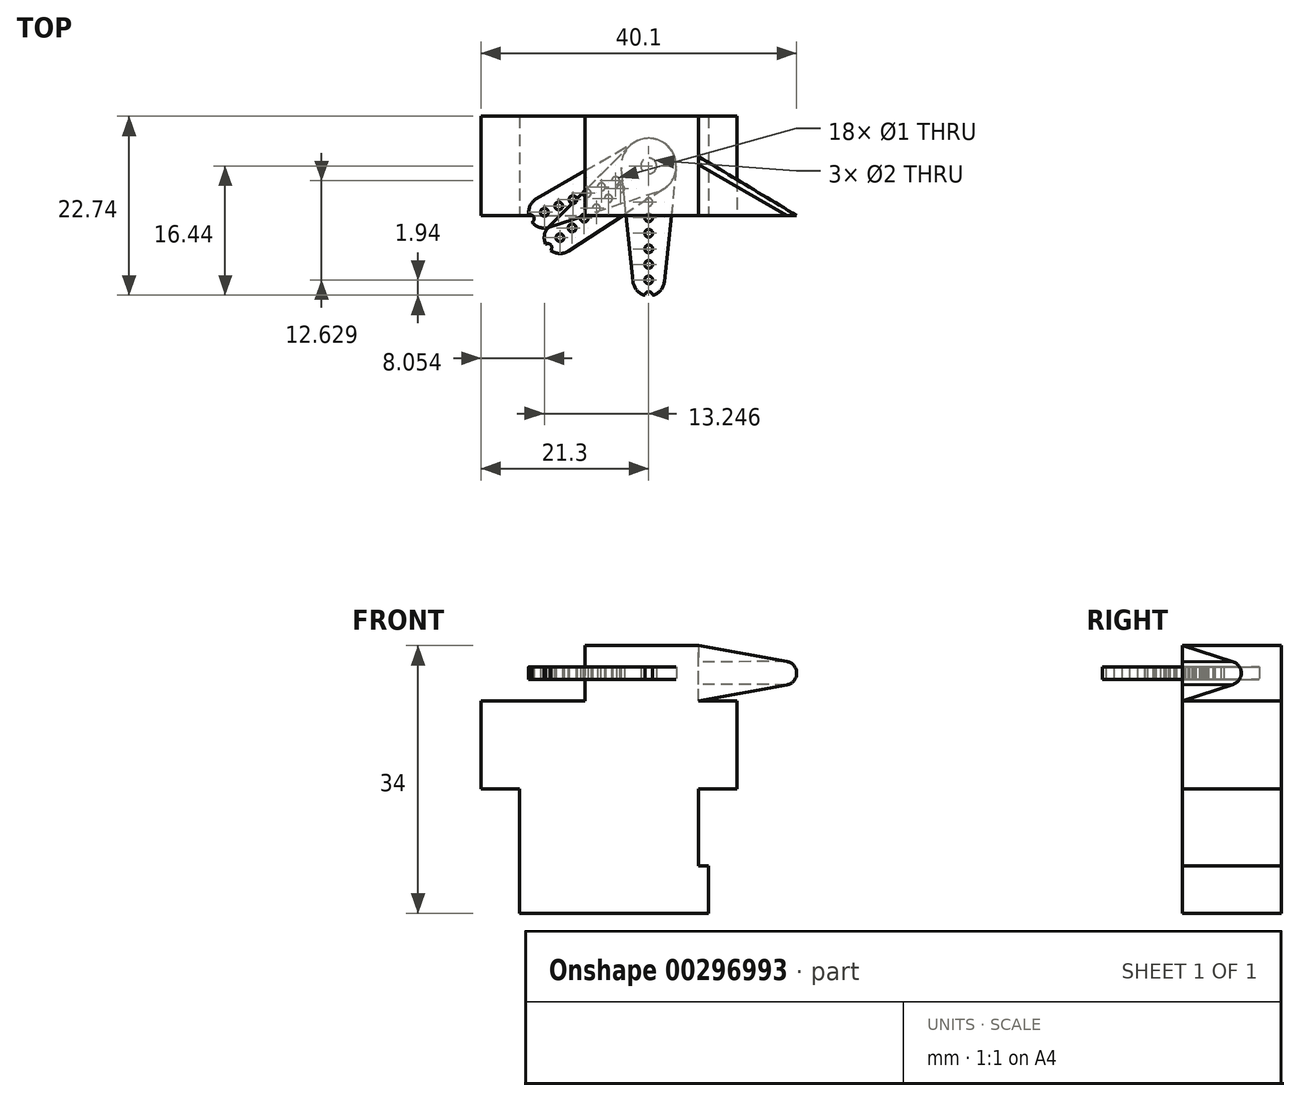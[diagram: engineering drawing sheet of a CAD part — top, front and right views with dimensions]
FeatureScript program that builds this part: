
annotation { "Feature Type Name" : "Feature", "Feature Type Description" : "" }
export const myFeature = defineFeature(function(context is Context, id is Id, definition is map)
    precondition{}
    {
        {
            var Q0;
            Q0=qCreatedBy(makeId("Front.planeOp"),FACE);
            var sketch = newSketch(context, id + "F0", { "sketchPlane" : qUnion([Q0])});
            skLineSegment(sketch, "E0.bottom", {"start": v(0, 6.8) * mm, "end": v(22.7, 6.8) * mm});
            skLineSegment(sketch, "E0.top", {"start": v(0, -15.8) * mm, "end": v(22.7, -15.8) * mm});
            skLineSegment(sketch, "E0.left", {"start": v(0, 6.8) * mm, "end": v(0, -15.8) * mm});
            skLineSegment(sketch, "E0.right", {"start": v(22.7, 6.8) * mm, "end": v(22.7, -15.8) * mm});
            skLineSegment(sketch, "E1.bottom", {"start": v(-4.9, 2.4) * mm, "end": v(27.6, 2.4) * mm});
            skLineSegment(sketch, "E1.top", {"start": v(-4.9, 0) * mm, "end": v(27.6, 0) * mm});
            skLineSegment(sketch, "E1.left", {"start": v(-4.9, 2.4) * mm, "end": v(-4.9, 0) * mm});
            skLineSegment(sketch, "E1.right", {"start": v(27.6, 2.4) * mm, "end": v(27.6, 0) * mm});
            skLineSegment(sketch, "E2.top", {"start": v(8.3, 6.8) * mm, "end": v(22.7, 6.8) * mm});
            skLineSegment(sketch, "E2.left", {"start": v(8.3, 11.2) * mm, "end": v(8.3, 6.8) * mm});
            skLineSegment(sketch, "E2.right", {"start": v(22.7, 11.2) * mm, "end": v(22.7, 6.8) * mm});
            skLineSegment(sketch, "E3", {"start": v(11.35, -15.8) * mm, "end": v(11.35, 0) * mm, "construction": true});
            skPoint(sketch, "E4", {"position": v(0, 0) * mm});
            skLineSegment(sketch, "E5", {"start": v(22.7, -15.8) * mm, "end": v(24, -15.8) * mm});
            skLineSegment(sketch, "E6", {"start": v(24, -15.8) * mm, "end": v(24, -9.8) * mm});
            skLineSegment(sketch, "E7", {"start": v(24, -9.8) * mm, "end": v(22.7, -9.8) * mm});
            skLineSegment(sketch, "E8", {"start": v(8.3, 18.2) * mm, "end": v(22.7, 18.2) * mm});
            skLineSegment(sketch, "E9", {"start": v(22.7, 18.2) * mm, "end": v(22.7, 11.2) * mm});
            skLineSegment(sketch, "E10", {"start": v(22.7, 11.2) * mm, "end": v(33.97, 13.22) * mm});
            skLineSegment(sketch, "E11", {"start": v(22.7, 18.2) * mm, "end": v(33.97, 16.18) * mm});
            skArc(sketch, "E12", {"start": v(33.97, 13.22) * mm, "mid": v(35.2, 14.7) * mm, "end": v(33.97, 16.18) * mm});
            skLineSegment(sketch, "E13", {"start": v(16.4, 14.7) * mm, "end": v(22.7, 14.7) * mm, "construction": true});
            skLineSegment(sketch, "E14", {"start": v(8.3, 11.2) * mm, "end": v(8.3, 18.2) * mm});
            skLineSegment(sketch, "E15", {"start": v(8.3, 11.2) * mm, "end": v(22.7, 11.2) * mm});
            skSolve(sketch);
        }
        {
            var Q0;
            {var subQ5=sQuery(id+"F0.wireOp",EDGE,"E0.bottom");Q0=makeQuery(id+"F0.imprint","IMPRINT",FACE,{"disambiguationData":[TD([[makeQuery(id+"F0.imprint","IMPRINT",EDGE,{"derivedFrom":subQ5}),-1.0]])]});}
            var Q1;
            {var subQ5=sQuery(id+"F0.wireOp",EDGE,"E1.left");Q1=makeQuery(id+"F0.imprint","IMPRINT",FACE,{"disambiguationData":[TD([[makeQuery(id+"F0.imprint","IMPRINT",EDGE,{"derivedFrom":subQ5}),1.0]])]});}
            var Q2;
            {var subQ0=sQuery(id+"F0.wireOp",EDGE,"E1.bottom");var subQ1=sQuery(id+"F0.wireOp",EDGE,"E0.left");var subQ2=makeQuery(id+"F0.imprint","INTERSECT",VERTEX,{"derivedFrom":[subQ1,subQ0]});Q2=makeQuery(id+"F0.imprint","IMPRINT",FACE,{"disambiguationData":[TD([[makeQuery(id+"F0.imprint","IMPRINT",EDGE,{"disambiguationData":[TD([[subQ2,-1.0]])],"derivedFrom":subQ1}),1.0]])]});}
            var Q3;
            Q3=makeQuery(id+"F0.imprint","IMPRINT",FACE,{"disambiguationData":[TD([[makeQuery(id+"F0.imprint","IMPRINT",EDGE,{"derivedFrom":sQuery(id+"F0.wireOp",EDGE,"E2.bottom")}),-1.0]])]});
            var Q4;
            {var subQ5=sQuery(id+"F0.wireOp",EDGE,"E1.right");Q4=makeQuery(id+"F0.imprint","IMPRINT",FACE,{"disambiguationData":[TD([[makeQuery(id+"F0.imprint","IMPRINT",EDGE,{"derivedFrom":subQ5}),-1.0]])]});}
            var Q5;
            {var subQ0=sQuery(id+"F0.wireOp",EDGE,"E0.top");Q5=makeQuery(id+"F0.imprint","IMPRINT",FACE,{"disambiguationData":[TD([[makeQuery(id+"F0.imprint","IMPRINT",EDGE,{"derivedFrom":subQ0}),1.0]])]});}
            var Q6;
            {var subQ0=sQuery(id+"F0.wireOp",EDGE,"E2.bottom");Q6=makeQuery(id+"F0.imprint","IMPRINT",FACE,{"disambiguationData":[TD([[makeQuery(id+"F0.imprint","IMPRINT",EDGE,{"derivedFrom":subQ0}),1.0]])]});}
            var Q7;
            Q7=makeQuery(id+"F0.imprint","IMPRINT",FACE,{"disambiguationData":[TD([[makeQuery(id+"F0.imprint","IMPRINT",EDGE,{"derivedFrom":sQuery(id+"F0.wireOp",EDGE,"E2.top")}),1.0]])]});
            extrude(context, id + "F1", {"entities" : qUnion([Q0, Q1, Q2, Q3, Q4, Q5, Q6, Q7]), "oppositeDirection" : true, "depth" : 12.6 * mm, "offsetDistance" : 25 * mm});
        }
        {
            var Q0;
            Q0=qCreatedBy(makeId("Top.planeOp"),FACE);
            var sketch = newSketch(context, id + "F2", { "sketchPlane" : qUnion([Q0])});
            skLineSegment(sketch, "E16.bottom", {"start": v(-4.9, 0) * mm, "end": v(27.6, 0) * mm});
            skLineSegment(sketch, "E16.top", {"start": v(-4.9, 12.6) * mm, "end": v(27.6, 12.6) * mm});
            skLineSegment(sketch, "E16.left", {"start": v(-4.9, 12.6) * mm, "end": v(-4.9, 0) * mm});
            skLineSegment(sketch, "E16.right", {"start": v(27.6, 12.6) * mm, "end": v(27.6, 0) * mm});
            skSolve(sketch);
        }
        {
            var Q0;
            Q0=qCreatedBy(makeId("Top.planeOp"),FACE);
            var Q1;
            Q1=sQuery(id+"F0.wireOp",VERTEX,"E13.start");
            cPlane(context, id + "F3", {"entities" : qUnion([Q0, Q1]), "cplaneType" : CPlaneType.PLANE_POINT, "offset" : 25 * mm, "width" : 150 * mm, "height" : 150 * mm});
        }
        {
            var Q0;
            Q0=qCreatedBy(id+"F3.planeOp",FACE);
            var sketch = newSketch(context, id + "F4", { "sketchPlane" : qUnion([Q0])});
            skLineSegment(sketch, "E17", {"start": v(16.4, 0) * mm, "end": v(16.4, 12.6) * mm, "construction": true});
            skPoint(sketch, "E18", {"position": v(16.4, 6.3) * mm});
            skPoint(sketch, "E19.0", {"position": v(16.4, 0) * mm});
            skLineSegment(sketch, "E20", {"start": v(16.4, 6.3) * mm, "end": v(16.4, -8.2) * mm});
            skLineSegment(sketch, "E21", {"start": v(16.4, 6.3) * mm, "end": v(16.4, 1.7) * mm});
            skCircle(sketch, "E22", {"center": v(16.4, 1.7) * mm, "radius": 0.5 * mm});
            skArc(sketch, "E23", {"start": v(18.39, -8.4) * mm, "mid": v(16.4, -10.2) * mm, "end": v(14.41, -8.4) * mm});
            skArc(sketch, "E24", {"start": v(19.88, 5.94) * mm, "mid": v(16.4, 9.8) * mm, "end": v(12.92, 5.94) * mm});
            skLineSegment(sketch, "E25", {"start": v(19.88, 5.94) * mm, "end": v(18.39, -8.4) * mm});
            skLineSegment(sketch, "E26", {"start": v(14.41, -8.4) * mm, "end": v(12.92, 5.94) * mm});
            skCircle(sketch, "E27", {"center": v(16.4, 6.3) * mm, "radius": 1 * mm});
            skCircle(sketch, "E28.1.0.0", {"center": v(16.4, -0.28) * mm, "radius": 0.5 * mm});
            skCircle(sketch, "E28.2.0.0", {"center": v(16.4, -2.26) * mm, "radius": 0.5 * mm});
            skLineSegment(sketch, "E28.direction1", {"start": v(16.4, 1.7) * mm, "end": v(16.4, -0.28) * mm, "construction": true});
            skCircle(sketch, "E29.0.3.0", {"center": v(16.4, -4.24) * mm, "radius": 0.5 * mm});
            skCircle(sketch, "E29.0.4.0", {"center": v(16.4, -6.22) * mm, "radius": 0.5 * mm});
            skCircle(sketch, "E29.0.5.0", {"center": v(16.4, -8.2) * mm, "radius": 0.5 * mm});
            skCircle(sketch, "E30.0.6.0", {"center": v(16.4, -10.18) * mm, "radius": 0.5 * mm});
            skLineSegment(sketch, "E31", {"start": v(16.4, 6.3) * mm, "end": v(3.15, 0.4) * mm, "construction": true});
            skLineSegment(sketch, "E32", {"start": v(16.4, 6.3) * mm, "end": v(5.13, -2.83) * mm, "construction": true});
            skSolve(sketch);
        }
        {
            var Q0;
            {var subQ1=sQuery(id+"F0.wireOp",EDGE,"E0.top");Q0=makeQuery(id+"F0.imprint","IMPRINT",FACE,{"disambiguationData":[TD([[makeQuery(id+"F0.imprint","IMPRINT",EDGE,{"derivedFrom":subQ1}),1.0]])]});}
            var Q1;
            {var subQ1=sQuery(id+"F0.wireOp",EDGE,"E0.bottom");Q1=makeQuery(id+"F0.imprint","IMPRINT",FACE,{"disambiguationData":[TD([[makeQuery(id+"F0.imprint","IMPRINT",EDGE,{"derivedFrom":subQ1}),-1.0]])]});}
            var Q2;
            {var subQ0=sQuery(id+"F0.wireOp",EDGE,"E1.bottom");var subQ1=sQuery(id+"F0.wireOp",EDGE,"E0.left");var subQ2=makeQuery(id+"F0.imprint","INTERSECT",VERTEX,{"derivedFrom":[subQ1,subQ0]});Q2=makeQuery(id+"F0.imprint","IMPRINT",FACE,{"disambiguationData":[TD([[makeQuery(id+"F0.imprint","IMPRINT",EDGE,{"disambiguationData":[TD([[subQ2,-1.0]])],"derivedFrom":subQ1}),1.0]])]});}
            var Q3;
            Q3=makeQuery(id+"F0.imprint","IMPRINT",FACE,{"disambiguationData":[TD([[makeQuery(id+"F0.imprint","IMPRINT",EDGE,{"derivedFrom":sQuery(id+"F0.wireOp",EDGE,"E2.bottom")}),-1.0]])]});
            var Q4;
            {var subQ0=sQuery(id+"F0.wireOp",EDGE,"E5");Q4=makeQuery(id+"F0.imprint","IMPRINT",FACE,{"disambiguationData":[TD([[makeQuery(id+"F0.imprint","IMPRINT",EDGE,{"derivedFrom":subQ0}),1.0]])]});}
            var Q5;
            {var subQ0=sQuery(id+"F0.wireOp",EDGE,"E9");var subQ5=sQuery(id+"F0.wireOp",EDGE,"E15");var subQ6=makeQuery(id+"F0.imprint","INTERSECT",VERTEX,{"derivedFrom":[subQ0,subQ5]});Q5=makeQuery(id+"F0.imprint","IMPRINT",FACE,{"disambiguationData":[TD([[makeQuery(id+"F0.imprint","IMPRINT",EDGE,{"disambiguationData":[TD([[subQ6,1.0]])],"derivedFrom":subQ5}),1.0]])]});}
            var Q6;
            {var subQ0=sQuery(id+"F0.wireOp",EDGE,"E9");var subQ5=sQuery(id+"F0.wireOp",EDGE,"E15");var subQ6=makeQuery(id+"F0.imprint","INTERSECT",VERTEX,{"derivedFrom":[subQ0,subQ5]});Q6=makeQuery(id+"F0.imprint","IMPRINT",FACE,{"disambiguationData":[TD([[makeQuery(id+"F0.imprint","IMPRINT",EDGE,{"disambiguationData":[TD([[subQ6,1.0]])],"derivedFrom":subQ5}),-1.0]])]});}
            var Q7;
            {var subQ0=sQuery(id+"F0.wireOp",EDGE,"E14");var subQ5=sQuery(id+"F0.wireOp",EDGE,"E15");var subQ6=makeQuery(id+"F0.imprint","INTERSECT",VERTEX,{"derivedFrom":[subQ0,subQ5]});Q7=makeQuery(id+"F0.imprint","IMPRINT",FACE,{"disambiguationData":[TD([[makeQuery(id+"F0.imprint","IMPRINT",EDGE,{"disambiguationData":[TD([[subQ6,-1.0]])],"derivedFrom":subQ5}),-1.0]])]});}
            var Q8;
            {var subQ0=sQuery(id+"F0.wireOp",EDGE,"E14");var subQ1=sQuery(id+"F0.wireOp",EDGE,"E8");var subQ2=makeQuery(id+"F0.imprint","INTERSECT",VERTEX,{"derivedFrom":[subQ1,subQ0]});Q8=makeQuery(id+"F0.imprint","IMPRINT",FACE,{"disambiguationData":[TD([[makeQuery(id+"F0.imprint","IMPRINT",EDGE,{"disambiguationData":[TD([[subQ2,-1.0]])],"derivedFrom":subQ1}),-1.0]])]});}
            var Q9;
            Q9=makeQuery(id+"F1.opExtrude","CAP_FACE",FACE,{"disambiguationData":[OSD([sQuery(id+"F0.wireOp",EDGE,"E0.bottom"),sQuery(id+"F0.wireOp",EDGE,"E0.top"),sQuery(id+"F0.wireOp",EDGE,"E0.left"),sQuery(id+"F0.wireOp",EDGE,"E0.right"),sQuery(id+"F0.wireOp",EDGE,"E1.bottom"),sQuery(id+"F0.wireOp",EDGE,"E1.top"),sQuery(id+"F0.wireOp",EDGE,"E1.left"),sQuery(id+"F0.wireOp",EDGE,"E1.right"),sQuery(id+"F0.wireOp",EDGE,"E2.bottom"),sQuery(id+"F0.wireOp",EDGE,"E2.left"),sQuery(id+"F0.wireOp",EDGE,"E2.right")])],"isStart":false});
            extrude(context, id + "F5", {"entities" : qUnion([Q0, Q1, Q2, Q3, Q4, Q5, Q6, Q7, Q8]), "endBound" : BoundingType.UP_TO_SURFACE, "oppositeDirection" : true, "depth" : 25 * mm, "endBoundEntityFace" : qUnion([Q9]), "offsetDistance" : 25 * mm});
        }
        {
            var Q0;
            Q0=makeQuery(id+"F5.opExtrude","SWEPT_BODY",BODY,{"disambiguationData":[OSD([sQuery(id+"F0.wireOp",EDGE,"E0.bottom"),sQuery(id+"F0.wireOp",EDGE,"E0.top"),sQuery(id+"F0.wireOp",EDGE,"E0.left"),sQuery(id+"F0.wireOp",EDGE,"E0.right"),sQuery(id+"F0.wireOp",EDGE,"E2.left"),sQuery(id+"F0.wireOp",EDGE,"E2.right"),sQuery(id+"F0.wireOp",EDGE,"E5"),sQuery(id+"F0.wireOp",EDGE,"E6"),sQuery(id+"F0.wireOp",EDGE,"E7"),sQuery(id+"F0.wireOp",EDGE,"E8"),sQuery(id+"F0.wireOp",EDGE,"E9"),sQuery(id+"F0.wireOp",EDGE,"E14")])]});
            transform(context, id + "F6", {"entities" : qUnion([Q0]), "transformType" : TransformType.COPY});
        }
        {
            var Q0;
            {var subQ0=sQuery(id+"F0.wireOp",EDGE,"E1.top");Q0=makeQuery(id+"F1.opExtrude","SWEPT_FACE",FACE,{"disambiguationData":[OSD([subQ0]),TDD([makeQuery(id+"F0.imprint","IMPRINT",EDGE,{"disambiguationData":[TD([[makeQuery(id+"F0.imprint","INTERSECT",VERTEX,{"derivedFrom":[subQ0,sQuery(id+"F0.wireOp",EDGE,"E1.left")]}),-1.0]])],"derivedFrom":subQ0})])]});}
            var Q1;
            {var subQ0=sQuery(id+"F0.wireOp",EDGE,"E1.top");Q1=makeQuery(id+"F1.opExtrude","SWEPT_FACE",FACE,{"disambiguationData":[OSD([subQ0]),TDD([makeQuery(id+"F0.imprint","IMPRINT",EDGE,{"disambiguationData":[TD([[makeQuery(id+"F0.imprint","INTERSECT",VERTEX,{"derivedFrom":[subQ0,sQuery(id+"F0.wireOp",EDGE,"E1.right")]}),1.0]])],"derivedFrom":subQ0})])]});}
            var Q2;
            Q2=makeQuery(id+"F1.opExtrude","SWEPT_FACE",FACE,{"disambiguationData":[OSD([sQuery(id+"F0.wireOp",EDGE,"E0.bottom")])]});
            var Q3;
            Q3=sQuery(id+"F0.wireOp",VERTEX,"E2.right.start");
            extrude(context, id + "F7", {"entities" : qUnion([Q0, Q1, Q2]), "operationType" : NewBodyOperationType.ADD, "endBound" : BoundingType.UP_TO_VERTEX, "oppositeDirection" : true, "depth" : 25 * mm, "endBoundEntityVertex" : qUnion([Q3]), "offsetDistance" : 25 * mm});
        }
        {
            var Q0;
            Q0=makeQuery(id+"F1.opExtrude","SWEPT_FACE",FACE,{"disambiguationData":[OSD([sQuery(id+"F0.wireOp",EDGE,"E0.right"),sQuery(id+"F0.wireOp",EDGE,"E2.right")])]});
            var sketch = newSketch(context, id + "F8", { "sketchPlane" : qUnion([Q0])});
            skLineSegment(sketch, "E33", {"start": v(0, 14.7) * mm, "end": v(6, 14.7) * mm, "construction": true});
            skLineSegment(sketch, "E34.0", {"start": v(0, 18.2) * mm, "end": v(0, 11.2) * mm});
            skLineSegment(sketch, "E35", {"start": v(0, 18.2) * mm, "end": v(6.46, 16.13) * mm});
            skLineSegment(sketch, "E36", {"start": v(0, 11.2) * mm, "end": v(6.46, 13.27) * mm});
            skArc(sketch, "E37", {"start": v(6.46, 16.13) * mm, "mid": v(7.5, 14.7) * mm, "end": v(6.46, 13.27) * mm});
            skPoint(sketch, "E38.0", {"position": v(0, 11.2) * mm});
            skSolve(sketch);
        }
        {
            var Q1;
            {var subQ1=sQuery(id+"F0.wireOp",EDGE,"E10");Q1=makeQuery(id+"F0.imprint","IMPRINT",FACE,{"disambiguationData":[TD([[makeQuery(id+"F0.imprint","IMPRINT",EDGE,{"derivedFrom":subQ1}),1.0]])]});}
            var Q2;
            {var subQ4=sQuery(id+"F8.wireOp",EDGE,"E35");Q2=makeQuery(id+"F8.imprint","IMPRINT",FACE,{"disambiguationData":[TD([[makeQuery(id+"F8.imprint","IMPRINT",EDGE,{"derivedFrom":subQ4}),-1.0]])]});}
            var Q3;
            Q3=sQuery(id+"F8.wireOp",VERTEX,"E35.end");
            var Q4;
            Q4=sQuery(id+"F0.wireOp",VERTEX,"E11.end");
            loft(context, id + "F9", {"operationType" : NewBodyOperationType.ADD, "sheetProfilesArray" : [{ "sheetProfileEntities" : qUnion([Q1]) }, { "sheetProfileEntities" : qUnion([Q2]) }], "matchConnections" : true, "connections" : [{ "connectionEntities" : qUnion([Q3, Q4]), "connectionEdgeQueries" : qUnion([]), "connectionEdgeParameters" : [] }]});
        }
        {
            var Q0;
            Q0=qCreatedBy(makeId("Right.planeOp"),FACE);
            var Q1;
            Q1=sQuery(id+"F0.wireOp",VERTEX,"E13.start");
            cPlane(context, id + "F10", {"entities" : qUnion([Q0, Q1]), "cplaneType" : CPlaneType.PLANE_POINT, "offset" : 25 * mm, "width" : 150 * mm, "height" : 150 * mm});
        }
        {
            var Q0;
            {var subQ1=sQuery(id+"F4.wireOp",EDGE,"E24");Q0=makeQuery(id+"F4.imprint","IMPRINT",FACE,{"disambiguationData":[TD([[makeQuery(id+"F4.imprint","IMPRINT",EDGE,{"derivedFrom":subQ1}),1.0]])]});}
            extrude(context, id + "F11", {"entities" : qUnion([Q0]), "endBound" : BoundingType.SYMMETRIC, "depth" : 1.6 * mm, "offsetDistance" : 25 * mm});
        }
        {
            var Q0;
            Q0=qCreatedBy(id+"F10.planeOp",FACE);
            var sketch = newSketch(context, id + "F12", { "sketchPlane" : qUnion([Q0])});
            skLineSegment(sketch, "E39", {"start": v(6.3, 14.7) * mm, "end": v(6.3, 21.7) * mm});
            skSolve(sketch);
        }
        {
            var Q0;
            Q0=makeQuery(id+"F11.opExtrude","SWEPT_BODY",BODY,{"disambiguationData":[OSD([sQuery(id+"F4.wireOp",EDGE,"E22"),sQuery(id+"F4.wireOp",EDGE,"E23"),sQuery(id+"F4.wireOp",EDGE,"E24"),sQuery(id+"F4.wireOp",EDGE,"E25"),sQuery(id+"F4.wireOp",EDGE,"E26"),sQuery(id+"F4.wireOp",EDGE,"E27"),sQuery(id+"F4.wireOp",EDGE,"E28.1.0.0"),sQuery(id+"F4.wireOp",EDGE,"E28.2.0.0"),sQuery(id+"F4.wireOp",EDGE,"E29.0.3.0"),sQuery(id+"F4.wireOp",EDGE,"E29.0.4.0"),sQuery(id+"F4.wireOp",EDGE,"E29.0.5.0"),sQuery(id+"F4.wireOp",EDGE,"E30.0.6.0")])]});
            var Q1;
            Q1=sQuery(id+"F12.wireOp",EDGE,"E39");
            transform(context, id + "F13", {"entities" : qUnion([Q0]), "transformType" : TransformType.ROTATION, "transformAxis" : qUnion([Q1]), "angle" : 51 * degree, "oppositeDirection" : true, "makeCopy" : true});
        }
        {
            var Q0;
            Q0=makeQuery(id+"F11.opExtrude","SWEPT_BODY",BODY,{"disambiguationData":[OSD([sQuery(id+"F4.wireOp",EDGE,"E22"),sQuery(id+"F4.wireOp",EDGE,"E23"),sQuery(id+"F4.wireOp",EDGE,"E24"),sQuery(id+"F4.wireOp",EDGE,"E25"),sQuery(id+"F4.wireOp",EDGE,"E26"),sQuery(id+"F4.wireOp",EDGE,"E27"),sQuery(id+"F4.wireOp",EDGE,"E28.1.0.0"),sQuery(id+"F4.wireOp",EDGE,"E28.2.0.0"),sQuery(id+"F4.wireOp",EDGE,"E29.0.3.0"),sQuery(id+"F4.wireOp",EDGE,"E29.0.4.0"),sQuery(id+"F4.wireOp",EDGE,"E29.0.5.0"),sQuery(id+"F4.wireOp",EDGE,"E30.0.6.0")])]});
            var Q1;
            Q1=sQuery(id+"F12.wireOp",EDGE,"E39");
            transform(context, id + "F14", {"entities" : qUnion([Q0]), "transformType" : TransformType.ROTATION, "transformAxis" : qUnion([Q1]), "angle" : 66 * degree, "oppositeDirection" : true, "makeCopy" : true});
        }
    });
